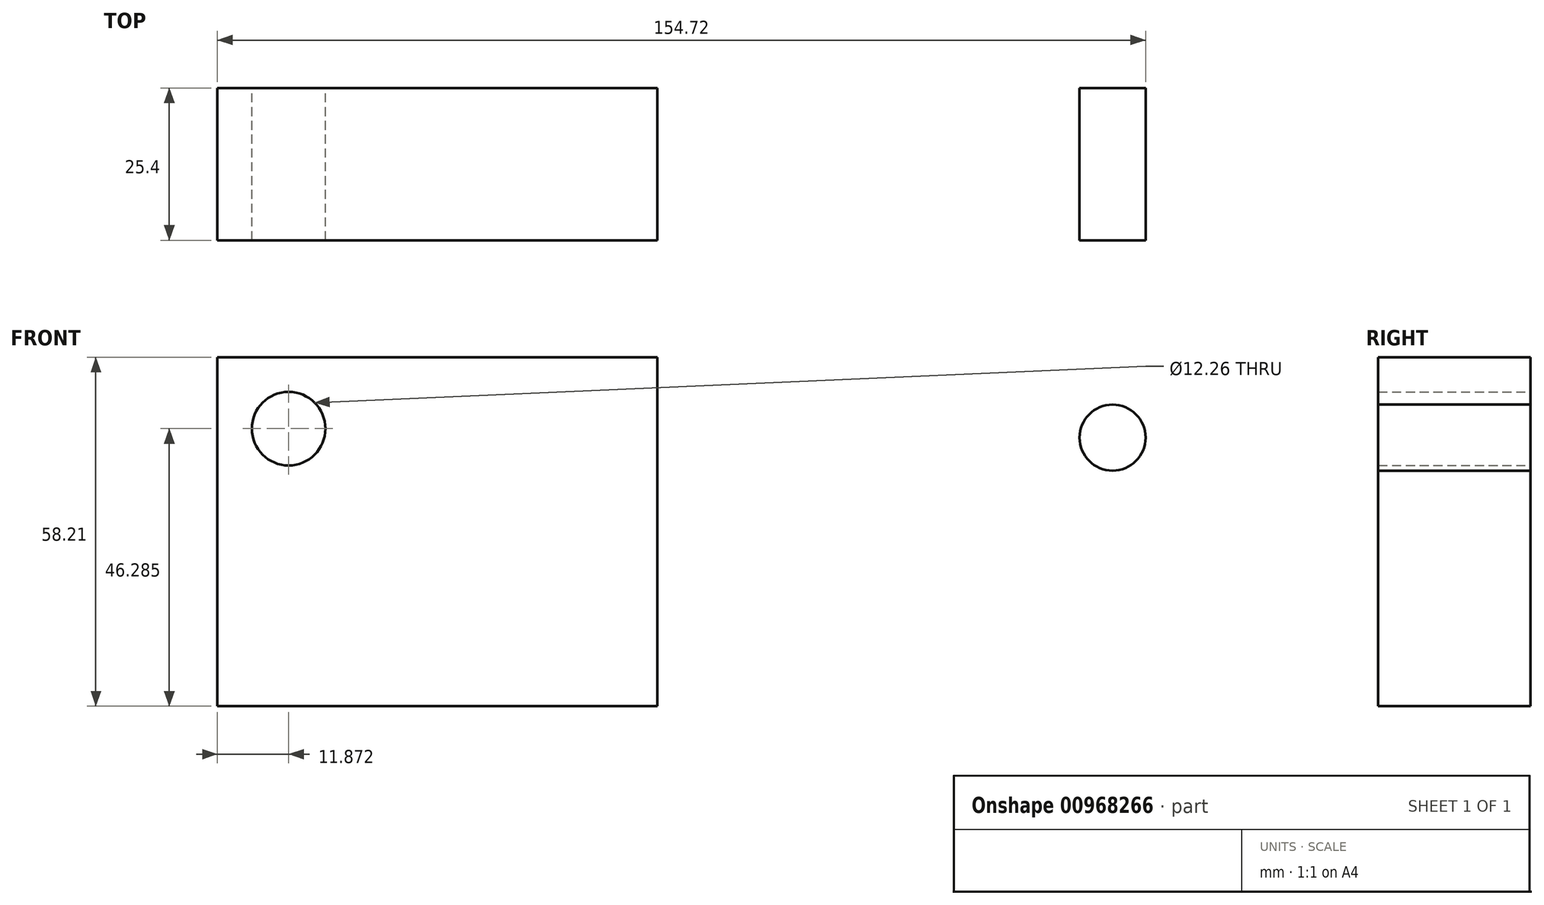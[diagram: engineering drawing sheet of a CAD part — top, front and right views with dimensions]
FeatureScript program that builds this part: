
annotation { "Feature Type Name" : "Feature", "Feature Type Description" : "" }
export const myFeature = defineFeature(function(context is Context, id is Id, definition is map)
    precondition{}
    {
        {
            var Q0;
            Q0=qCreatedBy(makeId("Front.planeOp"),FACE);
            var sketch = newSketch(context, id + "F0", { "sketchPlane" : qUnion([Q0])});
            skLineSegment(sketch, "E0.bottom", {"start": v(-56.3, 30.24) * mm, "end": v(17.02, 30.24) * mm});
            skLineSegment(sketch, "E0.top", {"start": v(-56.3, -27.97) * mm, "end": v(17.02, -27.97) * mm});
            skLineSegment(sketch, "E0.left", {"start": v(-56.3, 30.24) * mm, "end": v(-56.3, -27.97) * mm});
            skLineSegment(sketch, "E0.right", {"start": v(17.02, 30.24) * mm, "end": v(17.02, -27.97) * mm});
            skCircle(sketch, "E1", {"center": v(-44.44, 18.31) * mm, "radius": 6.13 * mm});
            skCircle(sketch, "E2", {"center": v(92.9, 16.82) * mm, "radius": 5.5 * mm});
            skSolve(sketch);
        }
        {
            var Q0;
            Q0=makeQuery(id+"F0.imprint","IMPRINT",FACE,{"disambiguationData":[TD([[makeQuery(id+"F0.imprint","IMPRINT",EDGE,{"derivedFrom":sQuery(id+"F0.wireOp",EDGE,"E0.bottom")}),-1.0]])]});
            var Q1;
            Q1=makeQuery(id+"F0.imprint","IMPRINT",FACE,{"disambiguationData":[TD([[makeQuery(id+"F0.imprint","IMPRINT",EDGE,{"derivedFrom":sQuery(id+"F0.wireOp",EDGE,"E2")}),1.0]])]});
            extrude(context, id + "F1", {"entities" : qUnion([Q0, Q1]), "depth" : 25.4 * mm, "offsetDistance" : 25.4 * mm});
        }
    });
